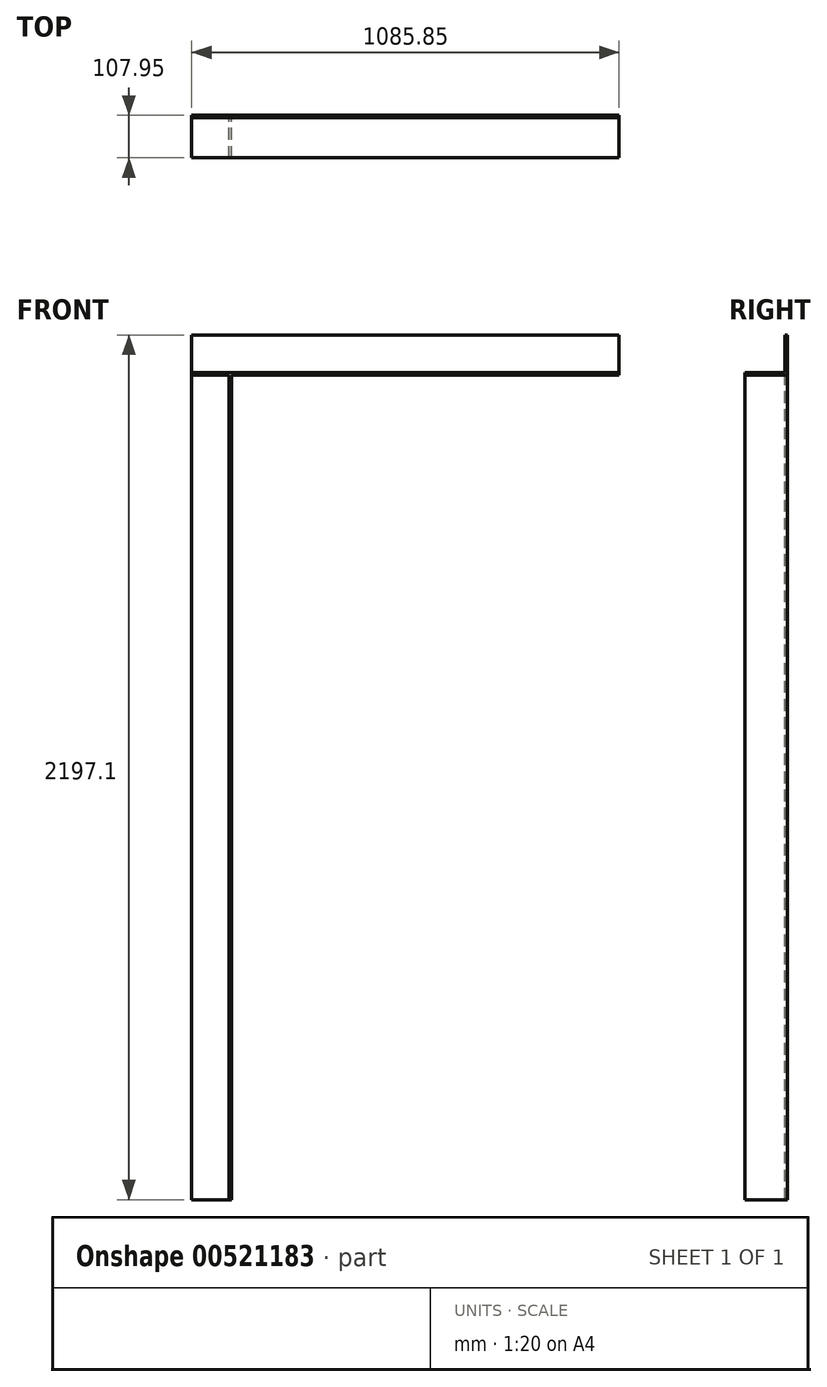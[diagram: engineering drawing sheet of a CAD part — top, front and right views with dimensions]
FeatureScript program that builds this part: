
annotation { "Feature Type Name" : "Feature", "Feature Type Description" : "" }
export const myFeature = defineFeature(function(context is Context, id is Id, definition is map)
    precondition{}
    {
        {
            var Q0;
            Q0=qCreatedBy(makeId("Front.planeOp"),FACE);
            var sketch = newSketch(context, id + "F0", { "sketchPlane" : qUnion([Q0])});
            skLineSegment(sketch, "E0.bottom", {"start": v(0, 0) * mm, "end": v(101.6, 0) * mm});
            skLineSegment(sketch, "E0.top", {"start": v(0, 2095.5) * mm, "end": v(101.6, 2095.5) * mm});
            skLineSegment(sketch, "E0.left", {"start": v(0, 0) * mm, "end": v(0, 2095.5) * mm});
            skLineSegment(sketch, "E0.right", {"start": v(101.6, 0) * mm, "end": v(101.6, 2095.5) * mm});
            skLineSegment(sketch, "E1.bottom", {"start": v(0, 2095.5) * mm, "end": v(1085.85, 2095.5) * mm});
            skLineSegment(sketch, "E1.top", {"start": v(0, 2197.1) * mm, "end": v(1085.85, 2197.1) * mm});
            skLineSegment(sketch, "E1.left", {"start": v(0, 2095.5) * mm, "end": v(0, 2197.1) * mm});
            skLineSegment(sketch, "E1.right", {"start": v(1085.85, 2095.5) * mm, "end": v(1085.85, 2197.1) * mm});
            skLineSegment(sketch, "E2.bottom", {"start": v(1085.85, 2095.5) * mm, "end": v(984.25, 2095.5) * mm});
            skLineSegment(sketch, "E2.top", {"start": v(1085.85, 0) * mm, "end": v(984.25, 0) * mm});
            skLineSegment(sketch, "E2.left", {"start": v(1085.85, 2095.5) * mm, "end": v(1085.85, 0) * mm});
            skLineSegment(sketch, "E2.right", {"start": v(984.25, 2095.5) * mm, "end": v(984.25, 0) * mm});
            skSolve(sketch);
        }
        {
            var Q0;
            Q0=makeQuery(id+"F0.imprint","IMPRINT",FACE,{"disambiguationData":[TD([[makeQuery(id+"F0.imprint","IMPRINT",EDGE,{"derivedFrom":sQuery(id+"F0.wireOp",EDGE,"E1.top")}),-1.0]])]});
            var Q1;
            Q1=makeQuery(id+"F0.imprint","IMPRINT",FACE,{"disambiguationData":[TD([[makeQuery(id+"F0.imprint","IMPRINT",EDGE,{"derivedFrom":sQuery(id+"F0.wireOp",EDGE,"E0.bottom")}),1.0]])]});
            var Q2;
            Q2=makeQuery(id+"F0.imprint","IMPRINT",FACE,{"disambiguationData":[TD([[makeQuery(id+"F0.imprint","IMPRINT",EDGE,{"derivedFrom":sQuery(id+"F0.wireOp",EDGE,"E2.bottom")}),1.0]])]});
            extrude(context, id + "F1", {"entities" : qUnion([Q0, Q1, Q2]), "depth" : 6.35 * mm, "offsetDistance" : 25.4 * mm});
        }
        {
            var Q0;
            Q0=makeQuery(id+"F1.opExtrude","CAP_FACE",FACE,{"disambiguationData":[OSD([sQuery(id+"F0.wireOp",EDGE,"E0.bottom"),sQuery(id+"F0.wireOp",EDGE,"E0.left"),sQuery(id+"F0.wireOp",EDGE,"E0.right"),sQuery(id+"F0.wireOp",EDGE,"E1.bottom"),sQuery(id+"F0.wireOp",EDGE,"E1.top"),sQuery(id+"F0.wireOp",EDGE,"E1.left"),sQuery(id+"F0.wireOp",EDGE,"E1.right"),sQuery(id+"F0.wireOp",EDGE,"E2.top"),sQuery(id+"F0.wireOp",EDGE,"E2.left"),sQuery(id+"F0.wireOp",EDGE,"E2.right")])],"isStart":false});
            var sketch = newSketch(context, id + "F2", { "sketchPlane" : qUnion([Q0])});
            skLineSegment(sketch, "E3.bottom", {"start": v(0, 2095.5) * mm, "end": v(1085.85, 2095.5) * mm});
            skLineSegment(sketch, "E3.top", {"start": v(0, 2101.85) * mm, "end": v(1085.85, 2101.85) * mm});
            skLineSegment(sketch, "E3.left", {"start": v(0, 2095.5) * mm, "end": v(0, 2101.85) * mm});
            skLineSegment(sketch, "E3.right", {"start": v(1085.85, 2095.5) * mm, "end": v(1085.85, 2101.85) * mm});
            skLineSegment(sketch, "E4.bottom", {"start": v(101.6, 0) * mm, "end": v(95.25, 0) * mm});
            skLineSegment(sketch, "E4.top", {"start": v(101.6, 2095.5) * mm, "end": v(95.25, 2095.5) * mm});
            skLineSegment(sketch, "E4.left", {"start": v(101.6, 0) * mm, "end": v(101.6, 2095.5) * mm});
            skLineSegment(sketch, "E4.right", {"start": v(95.25, 0) * mm, "end": v(95.25, 2095.5) * mm});
            skLineSegment(sketch, "E5.bottom", {"start": v(984.25, 2095.5) * mm, "end": v(990.6, 2095.5) * mm});
            skLineSegment(sketch, "E5.top", {"start": v(984.25, 0) * mm, "end": v(990.6, 0) * mm});
            skLineSegment(sketch, "E5.left", {"start": v(984.25, 2095.5) * mm, "end": v(984.25, 0) * mm});
            skLineSegment(sketch, "E5.right", {"start": v(990.6, 2095.5) * mm, "end": v(990.6, 0) * mm});
            skSolve(sketch);
        }
        {
            var Q0;
            Q0=makeQuery(id+"F2.imprint","IMPRINT",FACE,{"disambiguationData":[TD([[makeQuery(id+"F2.imprint","IMPRINT",EDGE,{"derivedFrom":sQuery(id+"F2.wireOp",EDGE,"E3.top")}),-1.0]])]});
            var Q1;
            Q1=makeQuery(id+"F2.imprint","IMPRINT",FACE,{"disambiguationData":[TD([[makeQuery(id+"F2.imprint","IMPRINT",EDGE,{"derivedFrom":sQuery(id+"F2.wireOp",EDGE,"E4.bottom")}),1.0]])]});
            var Q2;
            Q2=makeQuery(id+"F2.imprint","IMPRINT",FACE,{"disambiguationData":[TD([[makeQuery(id+"F2.imprint","IMPRINT",EDGE,{"derivedFrom":sQuery(id+"F2.wireOp",EDGE,"E5.bottom")}),-1.0]])]});
            extrude(context, id + "F3", {"entities" : qUnion([Q0, Q1, Q2]), "operationType" : NewBodyOperationType.ADD, "depth" : 101.6 * mm, "offsetDistance" : 25.4 * mm});
        }
    });
